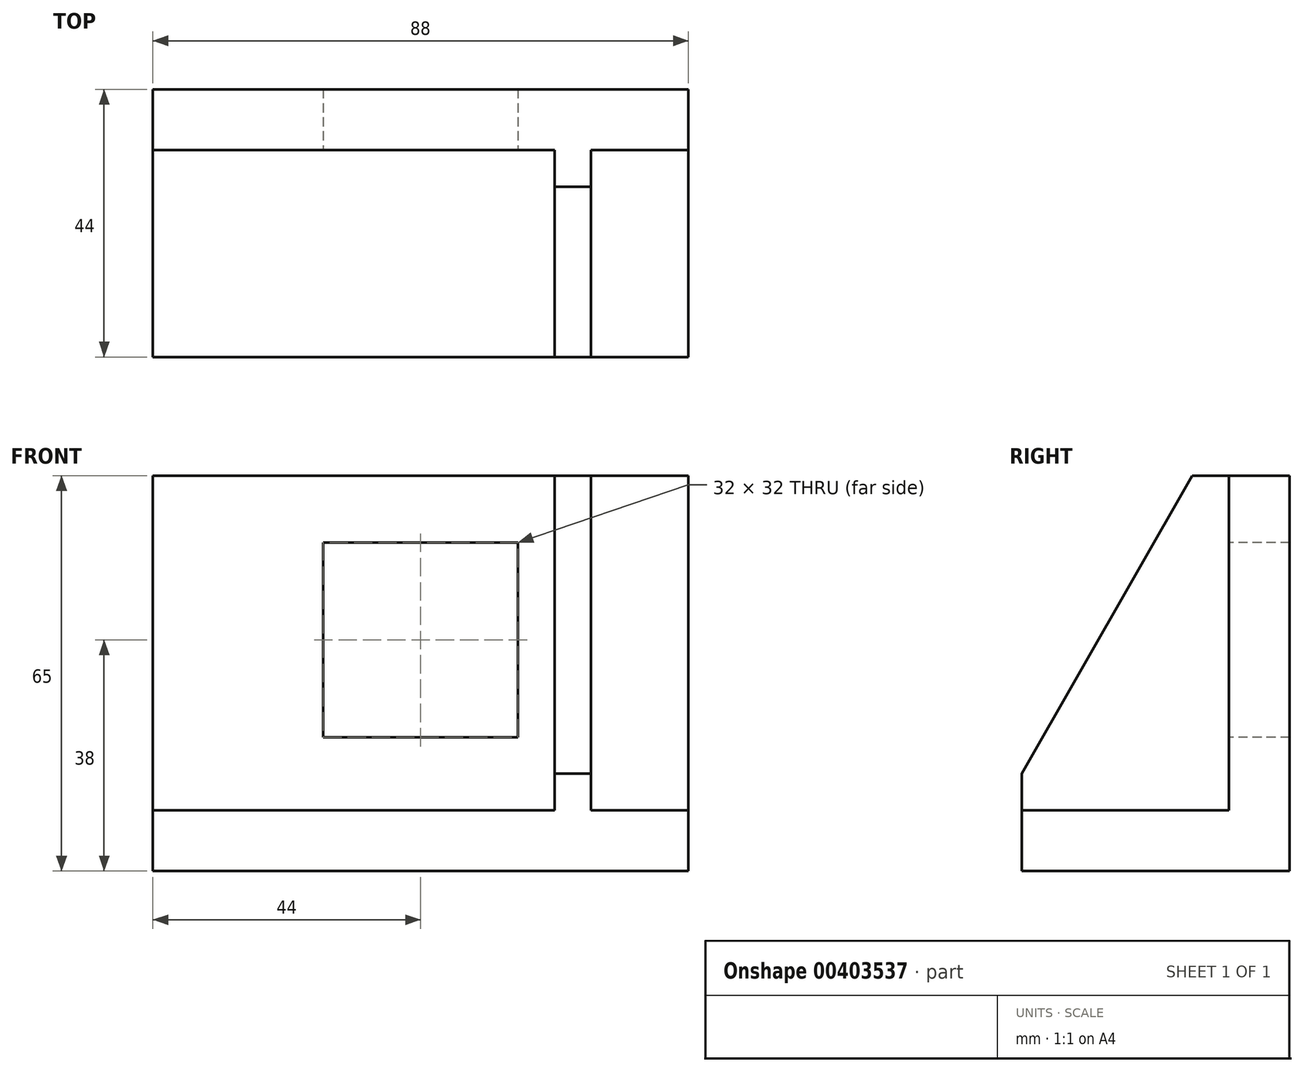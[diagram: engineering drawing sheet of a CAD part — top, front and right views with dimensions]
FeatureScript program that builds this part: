
annotation { "Feature Type Name" : "Feature", "Feature Type Description" : "" }
export const myFeature = defineFeature(function(context is Context, id is Id, definition is map)
    precondition{}
    {
        {
            var Q0;
            Q0=qCreatedBy(makeId("Right.planeOp"),FACE);
            var sketch = newSketch(context, id + "F0", { "sketchPlane" : qUnion([Q0])});
            skLineSegment(sketch, "E0", {"start": v(0, 0) * mm, "end": v(44, 0) * mm});
            skLineSegment(sketch, "E1", {"start": v(44, 0) * mm, "end": v(44, 65) * mm});
            skLineSegment(sketch, "E2", {"start": v(44, 65) * mm, "end": v(34, 65) * mm});
            skLineSegment(sketch, "E3", {"start": v(34, 65) * mm, "end": v(34, 10) * mm});
            skLineSegment(sketch, "E4", {"start": v(34, 10) * mm, "end": v(0, 10) * mm});
            skLineSegment(sketch, "E5", {"start": v(0, 10) * mm, "end": v(0, 0) * mm});
            skSolve(sketch);
        }
        {
            var Q0;
            Q0 = qSketchRegion(id + "F0", true);
            extrude(context, id + "F1", {"entities" : qUnion([Q0]), "endBound" : BoundingType.SYMMETRIC, "depth" : 88 * mm});
        }
        {
            var Q0;
            Q0=makeQuery(id+"F1.opExtrude","SWEPT_FACE",FACE,{"disambiguationData":[OSD([sQuery(id+"F0.wireOp",EDGE,"E3")])]});
            var sketch = newSketch(context, id + "F2", { "sketchPlane" : qUnion([Q0])});
            skLineSegment(sketch, "E6.bottom", {"start": v(16, 22) * mm, "end": v(-16, 22) * mm});
            skLineSegment(sketch, "E6.top", {"start": v(16, 54) * mm, "end": v(-16, 54) * mm});
            skLineSegment(sketch, "E6.left", {"start": v(16, 22) * mm, "end": v(16, 54) * mm});
            skLineSegment(sketch, "E6.right", {"start": v(-16, 22) * mm, "end": v(-16, 54) * mm});
            skPoint(sketch, "E6.middle", {"position": v(0, 38) * mm});
            skPoint(sketch, "E6.middle.positionSnap0", {"position": v(-44, 38) * mm});
            skPoint(sketch, "E6.middle.positionSnap1", {"position": v(0, 65) * mm});
            skPoint(sketch, "E6.centerSnap0", {"position": v(-44, 38) * mm});
            skPoint(sketch, "E6.centerSnap1", {"position": v(0, 65) * mm});
            skSolve(sketch);
        }
        {
            var Q0;
            Q0 = qSketchRegion(id + "F2", true);
            extrude(context, id + "F3", {"entities" : qUnion([Q0]), "operationType" : NewBodyOperationType.REMOVE, "endBound" : BoundingType.THROUGH_ALL, "oppositeDirection" : true, "depth" : 25 * mm});
        }
        {
            var Q0;
            Q0=makeQuery(id+"F1.opExtrude","CAP_FACE",FACE,{"disambiguationData":[OSD([sQuery(id+"F0.wireOp",EDGE,"E0"),sQuery(id+"F0.wireOp",EDGE,"E1"),sQuery(id+"F0.wireOp",EDGE,"E2"),sQuery(id+"F0.wireOp",EDGE,"E3"),sQuery(id+"F0.wireOp",EDGE,"E4"),sQuery(id+"F0.wireOp",EDGE,"E5")])],"isStart":false});
            cPlane(context, id + "F4", {"entities" : qUnion([Q0]), "cplaneType" : CPlaneType.OFFSET, "offset" : 19 * mm, "oppositeDirection" : true, "width" : 150 * mm, "height" : 150 * mm});
        }
        {
            var Q0;
            Q0=qCreatedBy(id+"F4.planeOp",FACE);
            var sketch = newSketch(context, id + "F5", { "sketchPlane" : qUnion([Q0])});
            skLineSegment(sketch, "E7", {"start": v(28, 65) * mm, "end": v(0, 16) * mm});
            skLineSegment(sketch, "E8", {"start": v(28, 65) * mm, "end": v(34, 65) * mm});
            skLineSegment(sketch, "E9", {"start": v(0, 16) * mm, "end": v(0, 10) * mm});
            skLineSegment(sketch, "E10", {"start": v(0, 10) * mm, "end": v(34, 10) * mm});
            skLineSegment(sketch, "E11", {"start": v(34, 10) * mm, "end": v(34, 65) * mm});
            skSolve(sketch);
        }
        {
            var Q0;
            Q0 = qSketchRegion(id + "F5", true);
            extrude(context, id + "F6", {"entities" : qUnion([Q0]), "operationType" : NewBodyOperationType.ADD, "endBound" : BoundingType.SYMMETRIC, "depth" : 6 * mm});
        }
    });
